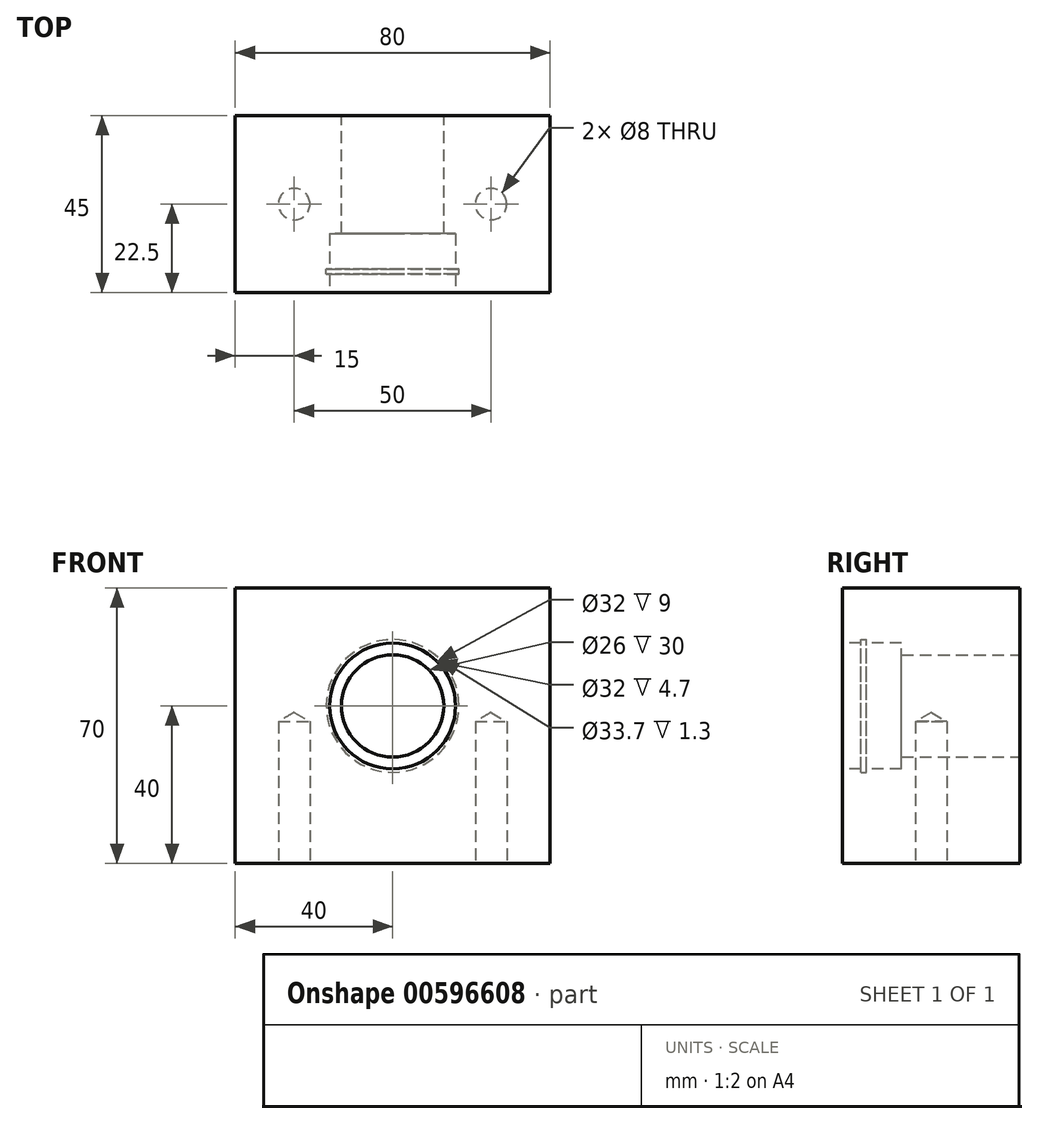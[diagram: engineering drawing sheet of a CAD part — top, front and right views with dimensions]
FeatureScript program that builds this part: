
annotation { "Feature Type Name" : "Feature", "Feature Type Description" : "" }
export const myFeature = defineFeature(function(context is Context, id is Id, definition is map)
    precondition{}
    {
        {
            var Q0;
            Q0=qCreatedBy(makeId("Front.planeOp"),FACE);
            var sketch = newSketch(context, id + "F0", { "sketchPlane" : qUnion([Q0])});
            skLineSegment(sketch, "E0.bottom", {"start": v(0, 0) * mm, "end": v(80, 0) * mm});
            skLineSegment(sketch, "E0.top", {"start": v(0, 70) * mm, "end": v(80, 70) * mm});
            skLineSegment(sketch, "E0.left", {"start": v(0, 0) * mm, "end": v(0, 70) * mm});
            skLineSegment(sketch, "E0.right", {"start": v(80, 0) * mm, "end": v(80, 70) * mm});
            skCircle(sketch, "E1", {"center": v(40, 40) * mm, "radius": 13 * mm});
            skSolve(sketch);
        }
        {
            var Q0;
            Q0 = qSketchRegion(id + "F0", true);
            extrude(context, id + "F1", {"entities" : qUnion([Q0]), "depth" : 45 * mm, "offsetDistance" : 25 * mm});
        }
        {
            var Q0;
            Q0=makeQuery(id+"F1.opExtrude","CAP_FACE",FACE,{"disambiguationData":[OSD([sQuery(id+"F0.wireOp",EDGE,"E0.bottom"),sQuery(id+"F0.wireOp",EDGE,"E0.top"),sQuery(id+"F0.wireOp",EDGE,"E0.left"),sQuery(id+"F0.wireOp",EDGE,"E0.right"),sQuery(id+"F0.wireOp",EDGE,"E1")])],"isStart":false});
            var sketch = newSketch(context, id + "F2", { "sketchPlane" : qUnion([Q0])});
            skCircle(sketch, "E2", {"center": v(40, 40) * mm, "radius": 16 * mm});
            skSolve(sketch);
        }
        {
            var Q0;
            Q0 = qSketchRegion(id + "F2", true);
            extrude(context, id + "F3", {"entities" : qUnion([Q0]), "operationType" : NewBodyOperationType.REMOVE, "oppositeDirection" : true, "depth" : 15 * mm, "offsetDistance" : 25 * mm});
        }
        {
            var Q0;
            Q0=makeQuery(id+"F3.boolean.opBoolean","COPY",FACE,{"derivedFrom":makeQuery(id+"F3.opExtrude","CAP_FACE",FACE,{"disambiguationData":[OSD([sQuery(id+"F2.wireOp",EDGE,"E2")])],"isStart":false})});
            cPlane(context, id + "F4", {"entities" : qUnion([Q0]), "cplaneType" : CPlaneType.OFFSET, "offset" : 9 * mm, "width" : 150 * mm, "height" : 150 * mm});
        }
        {
            var Q0;
            Q0=qCreatedBy(id+"F4.planeOp",FACE);
            var sketch = newSketch(context, id + "F5", { "sketchPlane" : qUnion([Q0])});
            skCircle(sketch, "E3", {"center": v(40, 40) * mm, "radius": 16.85 * mm});
            skSolve(sketch);
        }
        {
            var Q0;
            Q0 = qSketchRegion(id + "F5", true);
            extrude(context, id + "F6", {"entities" : qUnion([Q0]), "operationType" : NewBodyOperationType.REMOVE, "depth" : 1.3 * mm, "offsetDistance" : 25 * mm});
        }
        {
            var Q0;
            Q0=makeQuery(id+"F1.opExtrude","SWEPT_FACE",FACE,{"disambiguationData":[OSD([sQuery(id+"F0.wireOp",EDGE,"E0.bottom")])]});
            var sketch = newSketch(context, id + "F7", { "sketchPlane" : qUnion([Q0])});
            skPoint(sketch, "E4", {"position": v(15, 22.5) * mm});
            skPoint(sketch, "E5", {"position": v(65, 22.5) * mm});
            skSolve(sketch);
        }
        {
            var Q0;
            Q0=sQuery(id+"F7.wireOp",VERTEX,"E4");
            var Q1;
            Q1=sQuery(id+"F7.wireOp",VERTEX,"E5");
            var Q2;
            Q2=makeQuery(id+"F1.opExtrude","SWEPT_BODY",BODY,{"disambiguationData":[OSD([sQuery(id+"F0.wireOp",EDGE,"E0.bottom"),sQuery(id+"F0.wireOp",EDGE,"E0.top"),sQuery(id+"F0.wireOp",EDGE,"E0.left"),sQuery(id+"F0.wireOp",EDGE,"E0.right"),sQuery(id+"F0.wireOp",EDGE,"E1")])]});
            hole(context, id + "F8", {"style" : HoleStyle.C_BORE, "endStyle" : HoleEndStyle.BLIND, "holeDiameter" : 8 * mm, "cBoreDiameter" : 8 * mm, "cBoreDepth" : 0 * mm, "majorDiameter" : 5 * mm, "holeDepth" : 36 * mm, "isTappedThrough" : true, "tappedDepth" : 12 * mm, "tapClearance" : 3, "startFromSketch" : true, "locations" : qUnion([Q0, Q1]), "scope" : qUnion([Q2])});
        }
    });
